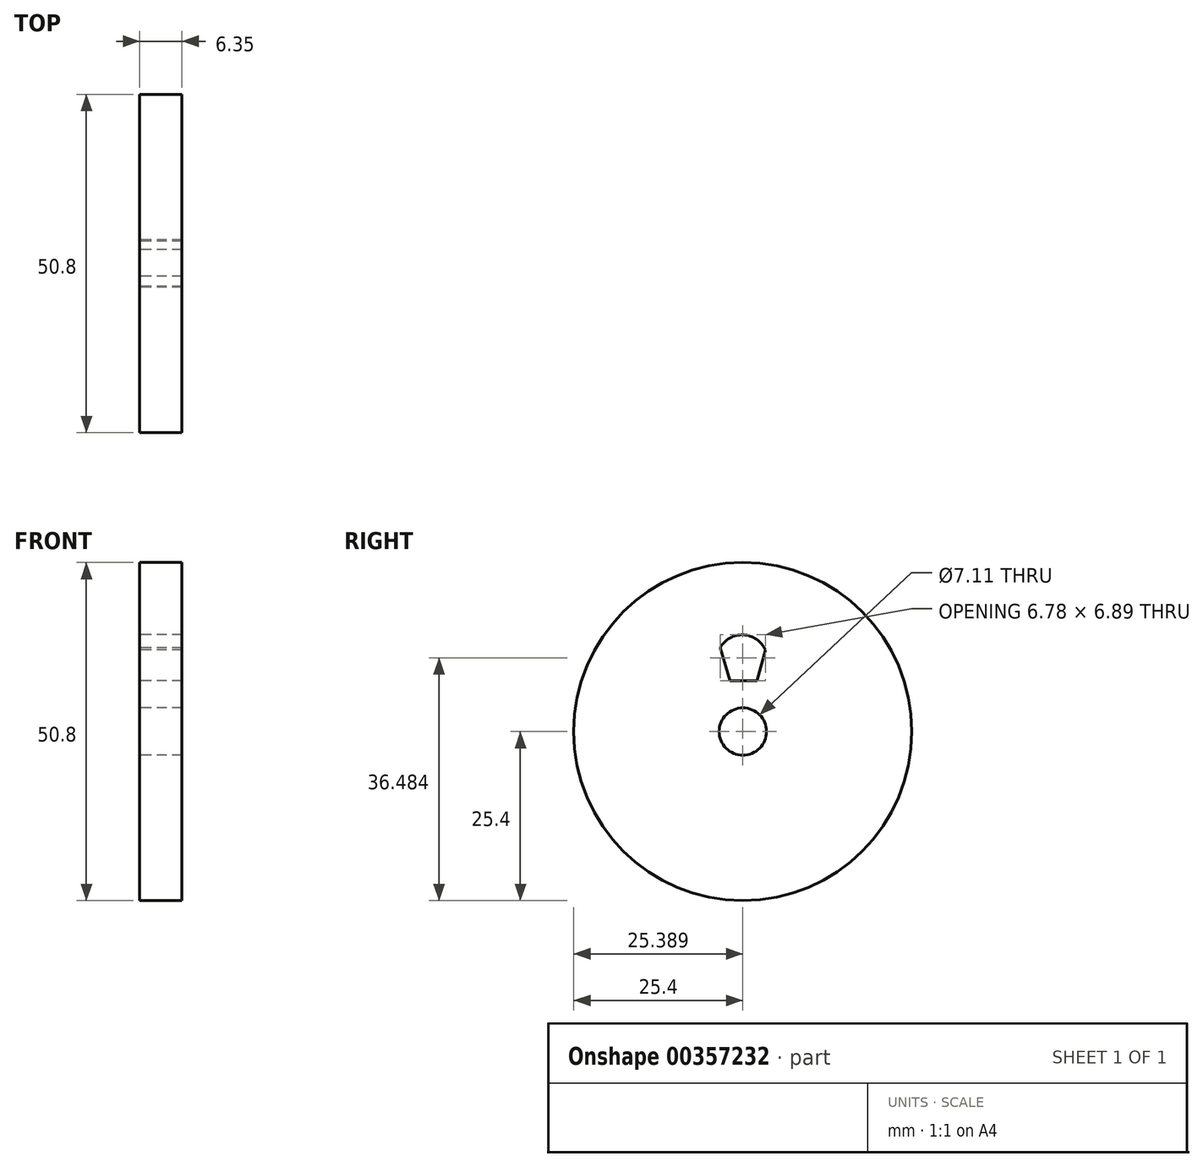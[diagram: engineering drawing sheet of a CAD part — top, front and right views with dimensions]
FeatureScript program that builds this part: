
annotation { "Feature Type Name" : "Feature", "Feature Type Description" : "" }
export const myFeature = defineFeature(function(context is Context, id is Id, definition is map)
    precondition{}
    {
        {
            var Q0;
            Q0=qCreatedBy(makeId("Right.planeOp"),FACE);
            var sketch = newSketch(context, id + "F0", { "sketchPlane" : qUnion([Q0])});
            skCircle(sketch, "E0", {"center": v(0, 0) * mm, "radius": 25.4 * mm});
            skCircle(sketch, "E1", {"center": v(0, 0) * mm, "radius": 3.56 * mm});
            skSolve(sketch);
        }
        {
            var Q0;
            Q0=makeQuery(id+"F0.imprint","IMPRINT",FACE,{"disambiguationData":[TD([[makeQuery(id+"F0.imprint","IMPRINT",EDGE,{"derivedFrom":sQuery(id+"F0.wireOp",EDGE,"E0")}),1.0]])]});
            extrude(context, id + "F1", {"entities" : qUnion([Q0]), "depth" : 6.35 * mm});
        }
        {
            var Q0;
            Q0=makeQuery(id+"F1.opExtrude","CAP_FACE",FACE,{"disambiguationData":[OSD([sQuery(id+"F0.wireOp",EDGE,"E0"),sQuery(id+"F0.wireOp",EDGE,"E1")])],"isStart":true});
            var sketch = newSketch(context, id + "F2", { "sketchPlane" : qUnion([Q0])});
            skLineSegment(sketch, "E2", {"start": v(-2.11, 7.64) * mm, "end": v(1.9, 7.64) * mm});
            skLineSegment(sketch, "E3", {"start": v(1.9, 7.64) * mm, "end": v(3.4, 12.58) * mm});
            skLineSegment(sketch, "E4", {"start": v(-2.11, 7.64) * mm, "end": v(-3.38, 12.23) * mm});
            skArc(sketch, "E5", {"start": v(3.4, 12.58) * mm, "mid": v(-0.1, 14.53) * mm, "end": v(-3.38, 12.23) * mm});
            skSolve(sketch);
        }
        {
            var Q0;
            Q0=makeQuery(id+"F2.imprint","IMPRINT",FACE,{"disambiguationData":[TD([[makeQuery(id+"F2.imprint","IMPRINT",EDGE,{"derivedFrom":sQuery(id+"F2.wireOp",EDGE,"E2")}),1.0]])]});
            extrude(context, id + "F3", {"entities" : qUnion([Q0]), "operationType" : NewBodyOperationType.REMOVE, "oppositeDirection" : true, "depth" : 76.2 * mm});
        }
    });
